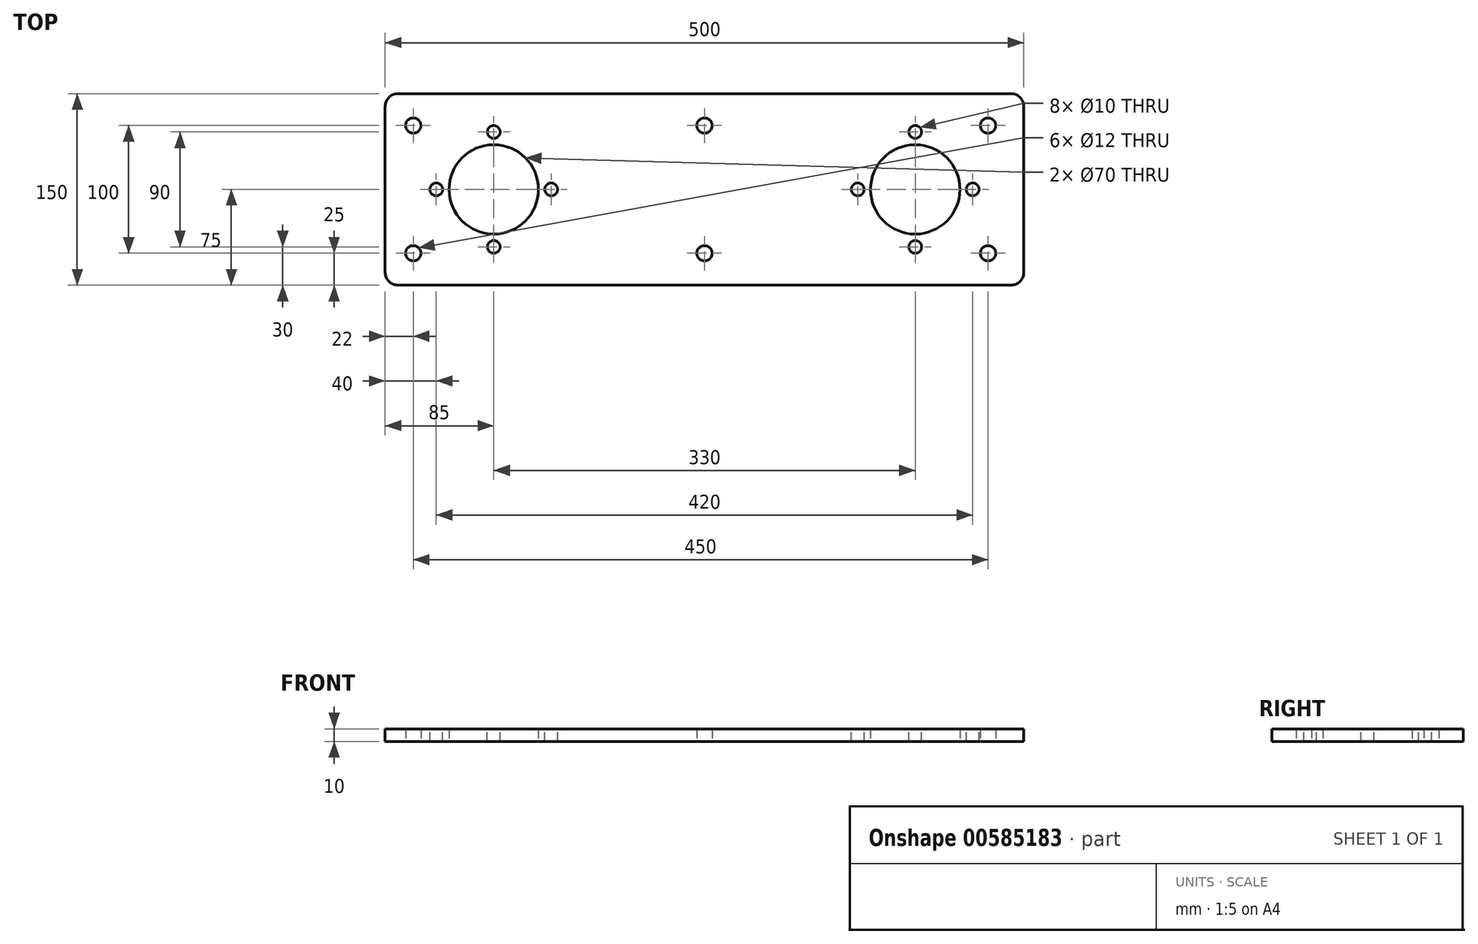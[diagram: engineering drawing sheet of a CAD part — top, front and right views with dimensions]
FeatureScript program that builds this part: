
annotation { "Feature Type Name" : "Feature", "Feature Type Description" : "" }
export const myFeature = defineFeature(function(context is Context, id is Id, definition is map)
    precondition{}
    {
        {
            var Q0;
            Q0=qCreatedBy(makeId("Top.planeOp"),FACE);
            var sketch = newSketch(context, id + "F0", { "sketchPlane" : qUnion([Q0])});
            skLineSegment(sketch, "E0.bottom", {"start": v(10, 0) * mm, "end": v(490, 0) * mm});
            skLineSegment(sketch, "E0.top", {"start": v(10, 150) * mm, "end": v(490, 150) * mm});
            skLineSegment(sketch, "E0.left", {"start": v(0, 10) * mm, "end": v(0, 140) * mm});
            skLineSegment(sketch, "E0.right", {"start": v(500, 10) * mm, "end": v(500, 140) * mm});
            skPoint(sketch, "E1.visualSharp", {"position": v(0, 150) * mm});
            skArc(sketch, "E1.filletArc", {"start": v(10, 150) * mm, "mid": v(2.93, 147.07) * mm, "end": v(0, 140) * mm});
            skPoint(sketch, "E2.visualSharp", {"position": v(500, 150) * mm});
            skArc(sketch, "E2.filletArc", {"start": v(500, 140) * mm, "mid": v(497.07, 147.07) * mm, "end": v(490, 150) * mm});
            skPoint(sketch, "E3.visualSharp", {"position": v(500, 0) * mm});
            skArc(sketch, "E3.filletArc", {"start": v(490, 0) * mm, "mid": v(497.07, 2.93) * mm, "end": v(500, 10) * mm});
            skPoint(sketch, "E4.visualSharp", {"position": v(0, 0) * mm});
            skArc(sketch, "E4.filletArc", {"start": v(0, 10) * mm, "mid": v(2.93, 2.93) * mm, "end": v(10, 0) * mm});
            skCircle(sketch, "E5", {"center": v(85, 75) * mm, "radius": 35 * mm});
            skCircle(sketch, "E6", {"center": v(415, 75) * mm, "radius": 35 * mm});
            skCircle(sketch, "E7", {"center": v(22, 125) * mm, "radius": 6 * mm});
            skCircle(sketch, "E8", {"center": v(472, 125) * mm, "radius": 6 * mm});
            skCircle(sketch, "E9", {"center": v(250, 125) * mm, "radius": 6 * mm});
            skCircle(sketch, "E10", {"center": v(472, 25) * mm, "radius": 6 * mm});
            skCircle(sketch, "E11", {"center": v(250, 25) * mm, "radius": 6 * mm});
            skCircle(sketch, "E12", {"center": v(22, 25) * mm, "radius": 6 * mm});
            skLineSegment(sketch, "E13.bottom", {"start": v(65, 0) * mm, "end": v(105, 0) * mm});
            skLineSegment(sketch, "E13.top", {"start": v(65, -15) * mm, "end": v(105, -15) * mm, "construction": true});
            skLineSegment(sketch, "E13.left", {"start": v(65, 0) * mm, "end": v(65, -15) * mm, "construction": true});
            skLineSegment(sketch, "E13.right", {"start": v(105, 0) * mm, "end": v(105, -15) * mm, "construction": true});
            skLineSegment(sketch, "E14.bottom", {"start": v(230, 0) * mm, "end": v(270, 0) * mm});
            skLineSegment(sketch, "E14.top", {"start": v(230, -15) * mm, "end": v(270, -15) * mm, "construction": true});
            skLineSegment(sketch, "E14.left", {"start": v(230, 0) * mm, "end": v(230, -15) * mm, "construction": true});
            skLineSegment(sketch, "E14.right", {"start": v(270, 0) * mm, "end": v(270, -15) * mm, "construction": true});
            skLineSegment(sketch, "E15.bottom", {"start": v(395, 0) * mm, "end": v(435, 0) * mm});
            skLineSegment(sketch, "E15.top", {"start": v(395, -15) * mm, "end": v(435, -15) * mm, "construction": true});
            skLineSegment(sketch, "E15.left", {"start": v(395, 0) * mm, "end": v(395, -15) * mm, "construction": true});
            skLineSegment(sketch, "E15.right", {"start": v(435, 0) * mm, "end": v(435, -15) * mm, "construction": true});
            skLineSegment(sketch, "E16.bottom", {"start": v(65, 150) * mm, "end": v(105, 150) * mm});
            skLineSegment(sketch, "E16.top", {"start": v(65, 165) * mm, "end": v(105, 165) * mm, "construction": true});
            skLineSegment(sketch, "E16.left", {"start": v(65, 150) * mm, "end": v(65, 165) * mm, "construction": true});
            skLineSegment(sketch, "E16.right", {"start": v(105, 150) * mm, "end": v(105, 165) * mm, "construction": true});
            skLineSegment(sketch, "E17.bottom", {"start": v(230, 150) * mm, "end": v(270, 150) * mm});
            skLineSegment(sketch, "E17.top", {"start": v(230, 165) * mm, "end": v(270, 165) * mm, "construction": true});
            skLineSegment(sketch, "E17.left", {"start": v(230, 150) * mm, "end": v(230, 165) * mm, "construction": true});
            skLineSegment(sketch, "E17.right", {"start": v(270, 150) * mm, "end": v(270, 165) * mm, "construction": true});
            skLineSegment(sketch, "E18.bottom", {"start": v(395, 150) * mm, "end": v(435, 150) * mm});
            skLineSegment(sketch, "E18.top", {"start": v(395, 165) * mm, "end": v(435, 165) * mm, "construction": true});
            skLineSegment(sketch, "E18.left", {"start": v(395, 150) * mm, "end": v(395, 165) * mm, "construction": true});
            skLineSegment(sketch, "E18.right", {"start": v(435, 150) * mm, "end": v(435, 165) * mm, "construction": true});
            skPoint(sketch, "E19", {"position": v(85, -15) * mm});
            skPoint(sketch, "E20", {"position": v(250, -15) * mm});
            skPoint(sketch, "E21", {"position": v(415, -15) * mm});
            skSolve(sketch);
        }
        {
            var Q0;
            Q0=qSketchRegion(id+"F0",true);
            extrude(context, id + "F1", {"entities" : qUnion([Q0]), "depth" : 10 * mm, "offsetDistance" : 25 * mm});
        }
        {
            var Q0;
            Q0=makeQuery(id+"F1.opExtrude","CAP_FACE",FACE,{"disambiguationData":[OSD([sQuery(id+"F0.wireOp",EDGE,"E0.bottom"),sQuery(id+"F0.wireOp",EDGE,"E0.top"),sQuery(id+"F0.wireOp",EDGE,"E0.left"),sQuery(id+"F0.wireOp",EDGE,"E0.right"),sQuery(id+"F0.wireOp",EDGE,"E1.filletArc"),sQuery(id+"F0.wireOp",EDGE,"E2.filletArc"),sQuery(id+"F0.wireOp",EDGE,"E3.filletArc"),sQuery(id+"F0.wireOp",EDGE,"E4.filletArc"),sQuery(id+"F0.wireOp",EDGE,"E5"),sQuery(id+"F0.wireOp",EDGE,"E6"),sQuery(id+"F0.wireOp",EDGE,"E7"),sQuery(id+"F0.wireOp",EDGE,"E8"),sQuery(id+"F0.wireOp",EDGE,"E9"),sQuery(id+"F0.wireOp",EDGE,"E10"),sQuery(id+"F0.wireOp",EDGE,"E11"),sQuery(id+"F0.wireOp",EDGE,"E12"),sQuery(id+"F0.wireOp",EDGE,"E13.bottom"),sQuery(id+"F0.wireOp",EDGE,"E14.bottom"),sQuery(id+"F0.wireOp",EDGE,"E15.bottom"),sQuery(id+"F0.wireOp",EDGE,"E16.bottom"),sQuery(id+"F0.wireOp",EDGE,"E17.bottom"),sQuery(id+"F0.wireOp",EDGE,"E18.bottom")])],"isStart":false});
            var sketch = newSketch(context, id + "F2", { "sketchPlane" : qUnion([Q0])});
            skCircle(sketch, "E22", {"center": v(85, 120) * mm, "radius": 5 * mm});
            skPoint(sketch, "E23", {"position": v(85, 75) * mm});
            skPoint(sketch, "E24", {"position": v(415, 75) * mm});
            skCircle(sketch, "E25", {"center": v(415, 120) * mm, "radius": 5 * mm});
            skCircle(sketch, "E26.1.0", {"center": v(40, 75) * mm, "radius": 5 * mm});
            skCircle(sketch, "E26.2.0", {"center": v(85, 30) * mm, "radius": 5 * mm});
            skCircle(sketch, "E26.3.0", {"center": v(130, 75) * mm, "radius": 5 * mm});
            skCircle(sketch, "E27.1.0", {"center": v(370, 75) * mm, "radius": 5 * mm});
            skCircle(sketch, "E27.2.0", {"center": v(415, 30) * mm, "radius": 5 * mm});
            skCircle(sketch, "E27.3.0", {"center": v(460, 75) * mm, "radius": 5 * mm});
            skSolve(sketch);
        }
        {
            var Q0;
            Q0 = qSketchRegion(id + "F2", true);
            extrude(context, id + "F3", {"entities" : qUnion([Q0]), "operationType" : NewBodyOperationType.REMOVE, "oppositeDirection" : true, "depth" : 25 * mm, "offsetDistance" : 25 * mm});
        }
    });
